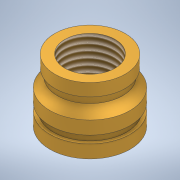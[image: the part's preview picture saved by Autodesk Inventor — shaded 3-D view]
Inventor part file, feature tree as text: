
AUTODESK INVENTOR PART (.ipt)
format: ipt  version: 2022 (Build 260153000, 153)  size: 166,400 bytes
history: native  units: mm
features: sketch x2, other x1, extrude x1, thread x1, revolve x1
ambient origin geometry x8: Origin, YZ Plane, XZ Plane, XY Plane, X Axis, Y Axis, Z Axis, Center Point
bodies: Body1 (feature_tree)
feature tree (6):
  other  "Твердое тело1"
  extrude  "Выдавливание1"  Depth=3.2mm
  thread  "Резьба1"
  revolve  "Вращение1"
  sketch  "Эскиз1"
  sketch  "Эскиз2"
